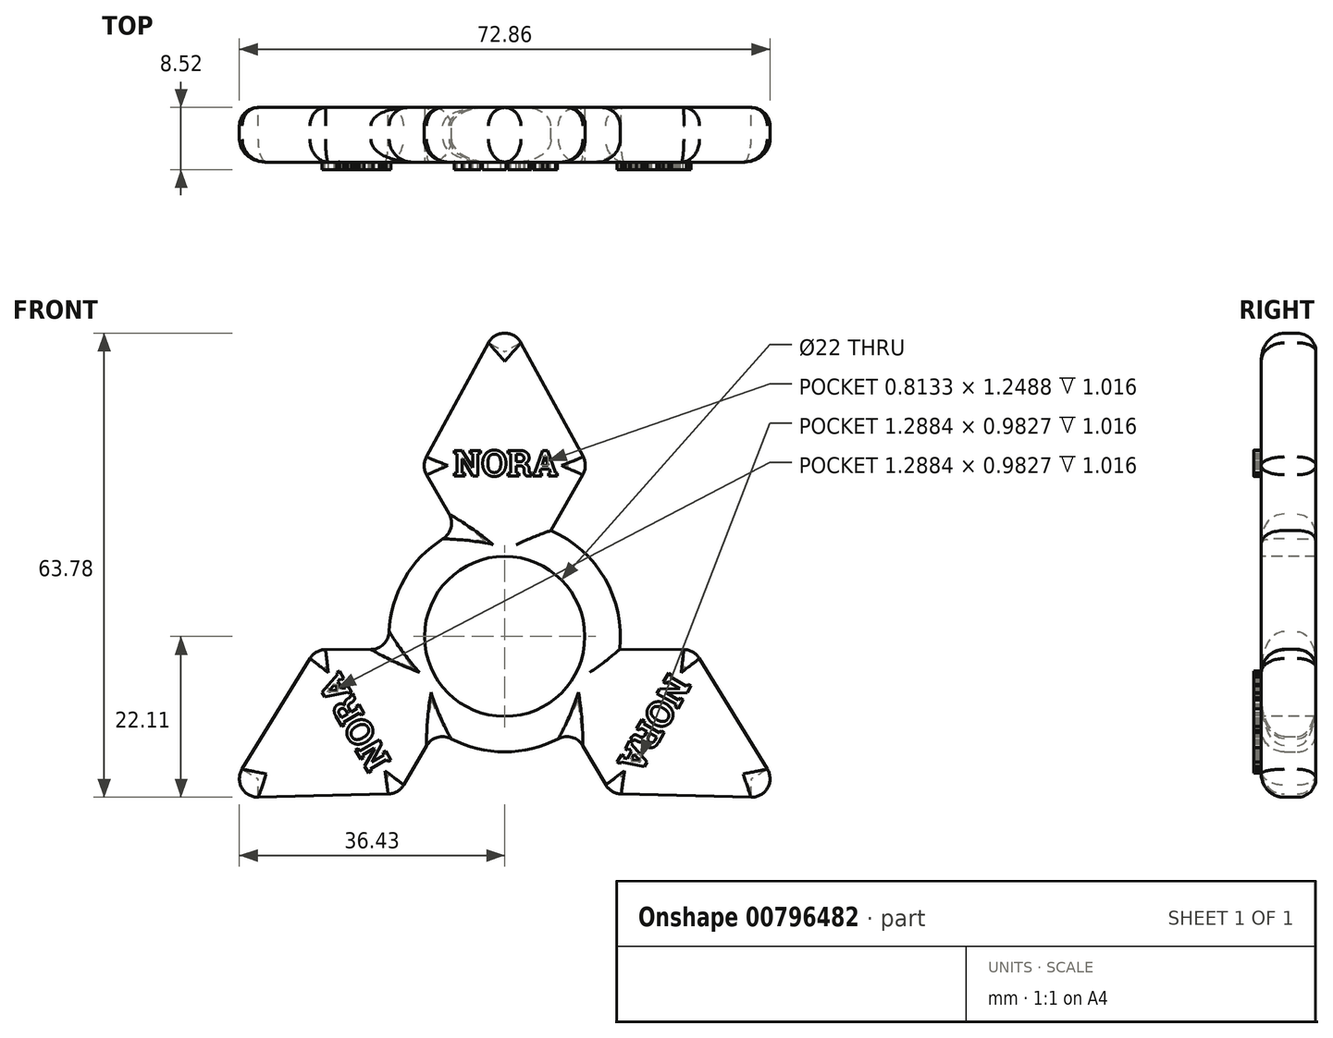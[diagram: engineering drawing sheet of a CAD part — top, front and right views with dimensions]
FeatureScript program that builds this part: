
annotation { "Feature Type Name" : "Feature", "Feature Type Description" : "" }
export const myFeature = defineFeature(function(context is Context, id is Id, definition is map)
    precondition{}
    {
        {
            var Q0;
            Q0=qCreatedBy(makeId("Front.planeOp"),FACE);
            var sketch = newSketch(context, id + "F0", { "sketchPlane" : qUnion([Q0])});
            skCircle(sketch, "E0", {"center": v(0, 0) * mm, "radius": 15.88 * mm});
            skSolve(sketch);
        }
        {
            var Q0;
            Q0 = qSketchRegion(id + "F0", true);
            extrude(context, id + "F1", {"entities" : qUnion([Q0]), "endBound" : BoundingType.SYMMETRIC, "depth" : 7.5 * mm, "offsetDistance" : 25.4 * mm});
        }
        {
            var Q0;
            Q0=qCreatedBy(makeId("Front.planeOp"),FACE);
            var sketch = newSketch(context, id + "F2", { "sketchPlane" : qUnion([Q0])});
            skLineSegment(sketch, "E1", {"start": v(-6.35, 14.55) * mm, "end": v(-11.43, 23.44) * mm});
            skLineSegment(sketch, "E2", {"start": v(-11.43, 23.44) * mm, "end": v(0, 44.45) * mm});
            skLineSegment(sketch, "E3", {"start": v(-17.44, 23.44) * mm, "end": v(16.7, 23.44) * mm, "construction": true});
            skLineSegment(sketch, "E4", {"start": v(0, 44.45) * mm, "end": v(11.43, 23.44) * mm});
            skLineSegment(sketch, "E5", {"start": v(11.43, 23.44) * mm, "end": v(6.35, 14.55) * mm});
            skLineSegment(sketch, "E6", {"start": v(0, 66.12) * mm, "end": v(0, -6.92) * mm, "construction": true});
            skLineSegment(sketch, "E7", {"start": v(-6.35, 14.55) * mm, "end": v(6.35, 14.55) * mm});
            skSolve(sketch);
        }
        {
            var Q0;
            Q0 = qSketchRegion(id + "F2", true);
            extrude(context, id + "F3", {"entities" : qUnion([Q0]), "endBound" : BoundingType.SYMMETRIC, "depth" : 7.5 * mm, "offsetDistance" : 25.4 * mm});
        }
        {
            var Q0;
            Q0=makeQuery(id+"F3.opExtrude","CAP_FACE",FACE,{"disambiguationData":[OSD([sQuery(id+"F2.wireOp",EDGE,"E1"),sQuery(id+"F2.wireOp",EDGE,"E2"),sQuery(id+"F2.wireOp",EDGE,"E4"),sQuery(id+"F2.wireOp",EDGE,"E5"),sQuery(id+"F2.wireOp",EDGE,"E7")])],"isStart":false});
            var sketch = newSketch(context, id + "F4", { "sketchPlane" : qUnion([Q0])});
            skText(sketch, "E8", { "text": "NORA", "fontName": "RobotoSlab-Bold.ttf"});
            const initialGuessF4  = {"E8": [-0.00705, 0.02202, 1, 0, 0.00359]};
            skSetInitialGuess(sketch, initialGuessF4);
            skSolve(sketch);
        }
        {
            var Q0;
            Q0 = qSketchRegion(id + "F4", true);
            extrude(context, id + "F5", {"entities" : qUnion([Q0]), "operationType" : NewBodyOperationType.ADD, "depth" : 1.02 * mm, "offsetDistance" : 25.4 * mm});
        }
        {
            var Q0;
            Q0=qCreatedBy(makeId("Top.planeOp"),FACE);
            var sketch = newSketch(context, id + "F6", { "sketchPlane" : qUnion([Q0])});
            skLineSegment(sketch, "E9", {"start": v(0, 50.9) * mm, "end": v(0, -46.74) * mm, "construction": true});
            skSolve(sketch);
        }
        {
            var Q0;
            Q0=makeQuery(id+"F3.opExtrude","SWEPT_BODY",BODY,{"disambiguationData":[OSD([sQuery(id+"F2.wireOp",EDGE,"E1"),sQuery(id+"F2.wireOp",EDGE,"E2"),sQuery(id+"F2.wireOp",EDGE,"E4"),sQuery(id+"F2.wireOp",EDGE,"E5"),sQuery(id+"F2.wireOp",EDGE,"E7")])]});
            var Q1;
            Q1=sQuery(id+"F6.wireOp",EDGE,"E9");
            circularPattern(context, id + "F7", {"entities" : qUnion([Q0]), "axis" : qUnion([Q1]), "angle" : 360 * degree, "instanceCount" : 3, "equalSpace" : true});
        }
        {
            var Q0;
            Q0=makeQuery(id+"F3.opExtrude","SWEPT_BODY",BODY,{"disambiguationData":[OSD([sQuery(id+"F2.wireOp",EDGE,"E1"),sQuery(id+"F2.wireOp",EDGE,"E2"),sQuery(id+"F2.wireOp",EDGE,"E4"),sQuery(id+"F2.wireOp",EDGE,"E5"),sQuery(id+"F2.wireOp",EDGE,"E7")])]});
            var Q1;
            Q1=makeQuery(id+"F1.opExtrude","SWEPT_BODY",BODY,{"disambiguationData":[OSD([sQuery(id+"F0.wireOp",EDGE,"E0")])]});
            var Q2;
            Q2=makeQuery(id+"F7.opPattern","COPY",BODY,{"derivedFrom":makeQuery(id+"F3.opExtrude","SWEPT_BODY",BODY,{"disambiguationData":[OSD([sQuery(id+"F2.wireOp",EDGE,"E1"),sQuery(id+"F2.wireOp",EDGE,"E2"),sQuery(id+"F2.wireOp",EDGE,"E4"),sQuery(id+"F2.wireOp",EDGE,"E5"),sQuery(id+"F2.wireOp",EDGE,"E7")])]}),"instanceName":"2"});
            var Q3;
            Q3=makeQuery(id+"F7.opPattern","COPY",BODY,{"derivedFrom":makeQuery(id+"F3.opExtrude","SWEPT_BODY",BODY,{"disambiguationData":[OSD([sQuery(id+"F2.wireOp",EDGE,"E1"),sQuery(id+"F2.wireOp",EDGE,"E2"),sQuery(id+"F2.wireOp",EDGE,"E4"),sQuery(id+"F2.wireOp",EDGE,"E5"),sQuery(id+"F2.wireOp",EDGE,"E7")])]}),"instanceName":"1"});
            booleanBodies(context, id + "F8", {"operationType" : BooleanOperationType.UNION, "tools" : qUnion([Q0, Q1, Q2, Q3])});
        }
        {
            var Q0;
            Q0=makeQuery(id+"F3.opExtrude","CAP_EDGE",EDGE,{"disambiguationData":[OSD([sQuery(id+"F2.wireOp",EDGE,"E4")])],"isStart":false});
            var Q1;
            Q1=makeQuery(id+"F3.opExtrude","CAP_EDGE",EDGE,{"disambiguationData":[OSD([sQuery(id+"F2.wireOp",EDGE,"E5")])],"isStart":false});
            var Q2;
            {var subQ0=sQuery(id+"F2.wireOp",EDGE,"E5");var subQ1=sQuery(id+"F0.wireOp",EDGE,"E0");Q2=makeQuery(id+"F8.opBoolean","SPLIT",EDGE,{"disambiguationData":[TD([makeQuery(id+"F3.opExtrude","SWEPT_FACE",FACE,{"disambiguationData":[OSD([subQ0])]})])],"derivedFrom":makeQuery(id+"F1.opExtrude","CAP_EDGE",EDGE,{"disambiguationData":[OSD([subQ1])],"isStart":false})});}
            var Q3;
            Q3=makeQuery(id+"F7.opPattern","COPY",EDGE,{"derivedFrom":makeQuery(id+"F3.opExtrude","CAP_EDGE",EDGE,{"disambiguationData":[OSD([sQuery(id+"F2.wireOp",EDGE,"E1")])],"isStart":false}),"instanceName":"2"});
            var Q4;
            Q4=makeQuery(id+"F7.opPattern","COPY",EDGE,{"derivedFrom":makeQuery(id+"F3.opExtrude","CAP_EDGE",EDGE,{"disambiguationData":[OSD([sQuery(id+"F2.wireOp",EDGE,"E2")])],"isStart":false}),"instanceName":"2"});
            var Q5;
            Q5=makeQuery(id+"F7.opPattern","COPY",EDGE,{"derivedFrom":makeQuery(id+"F3.opExtrude","CAP_EDGE",EDGE,{"disambiguationData":[OSD([sQuery(id+"F2.wireOp",EDGE,"E4")])],"isStart":false}),"instanceName":"2"});
            var Q6;
            Q6=makeQuery(id+"F7.opPattern","COPY",EDGE,{"derivedFrom":makeQuery(id+"F3.opExtrude","CAP_EDGE",EDGE,{"disambiguationData":[OSD([sQuery(id+"F2.wireOp",EDGE,"E5")])],"isStart":false}),"instanceName":"2"});
            var Q7;
            {var subQ0=sQuery(id+"F0.wireOp",EDGE,"E0");var subQ1=sQuery(id+"F2.wireOp",EDGE,"E1");Q7=makeQuery(id+"F8.opBoolean","SPLIT",EDGE,{"disambiguationData":[TD([makeQuery(id+"F7.opPattern","COPY",FACE,{"derivedFrom":makeQuery(id+"F3.opExtrude","SWEPT_FACE",FACE,{"disambiguationData":[OSD([subQ1])]}),"instanceName":"1"})])],"derivedFrom":makeQuery(id+"F1.opExtrude","CAP_EDGE",EDGE,{"disambiguationData":[OSD([subQ0])],"isStart":false})});}
            var Q8;
            Q8=makeQuery(id+"F7.opPattern","COPY",EDGE,{"derivedFrom":makeQuery(id+"F3.opExtrude","CAP_EDGE",EDGE,{"disambiguationData":[OSD([sQuery(id+"F2.wireOp",EDGE,"E1")])],"isStart":false}),"instanceName":"1"});
            var Q9;
            Q9=makeQuery(id+"F7.opPattern","COPY",EDGE,{"derivedFrom":makeQuery(id+"F3.opExtrude","CAP_EDGE",EDGE,{"disambiguationData":[OSD([sQuery(id+"F2.wireOp",EDGE,"E2")])],"isStart":false}),"instanceName":"1"});
            var Q10;
            Q10=makeQuery(id+"F7.opPattern","COPY",EDGE,{"derivedFrom":makeQuery(id+"F3.opExtrude","CAP_EDGE",EDGE,{"disambiguationData":[OSD([sQuery(id+"F2.wireOp",EDGE,"E4")])],"isStart":false}),"instanceName":"1"});
            var Q11;
            Q11=makeQuery(id+"F7.opPattern","COPY",EDGE,{"derivedFrom":makeQuery(id+"F3.opExtrude","CAP_EDGE",EDGE,{"disambiguationData":[OSD([sQuery(id+"F2.wireOp",EDGE,"E5")])],"isStart":false}),"instanceName":"1"});
            var Q12;
            {var subQ0=sQuery(id+"F2.wireOp",EDGE,"E1");var subQ1=sQuery(id+"F0.wireOp",EDGE,"E0");Q12=makeQuery(id+"F8.opBoolean","SPLIT",EDGE,{"disambiguationData":[TD([makeQuery(id+"F3.opExtrude","SWEPT_FACE",FACE,{"disambiguationData":[OSD([subQ0])]})])],"derivedFrom":makeQuery(id+"F1.opExtrude","CAP_EDGE",EDGE,{"disambiguationData":[OSD([subQ1])],"isStart":false})});}
            var Q13;
            Q13=makeQuery(id+"F3.opExtrude","CAP_EDGE",EDGE,{"disambiguationData":[OSD([sQuery(id+"F2.wireOp",EDGE,"E1")])],"isStart":false});
            var Q14;
            Q14=makeQuery(id+"F3.opExtrude","CAP_EDGE",EDGE,{"disambiguationData":[OSD([sQuery(id+"F2.wireOp",EDGE,"E2")])],"isStart":false});
            fillet(context, id + "F9", {"entities" : qUnion([Q0, Q1, Q2, Q3, Q4, Q5, Q6, Q7, Q8, Q9, Q10, Q11, Q12, Q13, Q14]), "radius" : 3.17 * mm, "tangentPropagation" : true, "allowEdgeOverflow" : false});
        }
        {
            var Q0;
            Q0=makeQuery(id+"F3.opExtrude","CAP_EDGE",EDGE,{"disambiguationData":[OSD([sQuery(id+"F2.wireOp",EDGE,"E2")])],"isStart":true});
            var Q1;
            Q1=makeQuery(id+"F3.opExtrude","CAP_EDGE",EDGE,{"disambiguationData":[OSD([sQuery(id+"F2.wireOp",EDGE,"E1")])],"isStart":true});
            var Q2;
            {var subQ1=sQuery(id+"F2.wireOp",EDGE,"E1");var subQ3=sQuery(id+"F0.wireOp",EDGE,"E0");Q2=makeQuery(id+"F8.opBoolean","SPLIT",EDGE,{"disambiguationData":[TD([makeQuery(id+"F3.opExtrude","SWEPT_FACE",FACE,{"disambiguationData":[OSD([subQ1])]})])],"derivedFrom":makeQuery(id+"F1.opExtrude","CAP_EDGE",EDGE,{"disambiguationData":[OSD([subQ3])],"isStart":true})});}
            var Q3;
            Q3=makeQuery(id+"F7.opPattern","COPY",EDGE,{"derivedFrom":makeQuery(id+"F3.opExtrude","CAP_EDGE",EDGE,{"disambiguationData":[OSD([sQuery(id+"F2.wireOp",EDGE,"E5")])],"isStart":true}),"instanceName":"1"});
            var Q4;
            Q4=makeQuery(id+"F7.opPattern","COPY",EDGE,{"derivedFrom":makeQuery(id+"F3.opExtrude","CAP_EDGE",EDGE,{"disambiguationData":[OSD([sQuery(id+"F2.wireOp",EDGE,"E4")])],"isStart":true}),"instanceName":"1"});
            var Q5;
            Q5=makeQuery(id+"F7.opPattern","COPY",EDGE,{"derivedFrom":makeQuery(id+"F3.opExtrude","CAP_EDGE",EDGE,{"disambiguationData":[OSD([sQuery(id+"F2.wireOp",EDGE,"E2")])],"isStart":true}),"instanceName":"1"});
            var Q6;
            Q6=makeQuery(id+"F7.opPattern","COPY",EDGE,{"derivedFrom":makeQuery(id+"F3.opExtrude","CAP_EDGE",EDGE,{"disambiguationData":[OSD([sQuery(id+"F2.wireOp",EDGE,"E1")])],"isStart":true}),"instanceName":"1"});
            var Q7;
            {var subQ0=sQuery(id+"F2.wireOp",EDGE,"E1");var subQ3=sQuery(id+"F0.wireOp",EDGE,"E0");Q7=makeQuery(id+"F8.opBoolean","SPLIT",EDGE,{"disambiguationData":[TD([makeQuery(id+"F7.opPattern","COPY",FACE,{"derivedFrom":makeQuery(id+"F3.opExtrude","SWEPT_FACE",FACE,{"disambiguationData":[OSD([subQ0])]}),"instanceName":"1"})])],"derivedFrom":makeQuery(id+"F1.opExtrude","CAP_EDGE",EDGE,{"disambiguationData":[OSD([subQ3])],"isStart":true})});}
            var Q8;
            Q8=makeQuery(id+"F7.opPattern","COPY",EDGE,{"derivedFrom":makeQuery(id+"F3.opExtrude","CAP_EDGE",EDGE,{"disambiguationData":[OSD([sQuery(id+"F2.wireOp",EDGE,"E5")])],"isStart":true}),"instanceName":"2"});
            var Q9;
            Q9=makeQuery(id+"F7.opPattern","COPY",EDGE,{"derivedFrom":makeQuery(id+"F3.opExtrude","CAP_EDGE",EDGE,{"disambiguationData":[OSD([sQuery(id+"F2.wireOp",EDGE,"E4")])],"isStart":true}),"instanceName":"2"});
            var Q10;
            Q10=makeQuery(id+"F7.opPattern","COPY",EDGE,{"derivedFrom":makeQuery(id+"F3.opExtrude","CAP_EDGE",EDGE,{"disambiguationData":[OSD([sQuery(id+"F2.wireOp",EDGE,"E2")])],"isStart":true}),"instanceName":"2"});
            var Q11;
            Q11=makeQuery(id+"F7.opPattern","COPY",EDGE,{"derivedFrom":makeQuery(id+"F3.opExtrude","CAP_EDGE",EDGE,{"disambiguationData":[OSD([sQuery(id+"F2.wireOp",EDGE,"E1")])],"isStart":true}),"instanceName":"2"});
            var Q12;
            {var subQ0=sQuery(id+"F2.wireOp",EDGE,"E5");var subQ3=sQuery(id+"F0.wireOp",EDGE,"E0");Q12=makeQuery(id+"F8.opBoolean","SPLIT",EDGE,{"disambiguationData":[TD([makeQuery(id+"F3.opExtrude","SWEPT_FACE",FACE,{"disambiguationData":[OSD([subQ0])]})])],"derivedFrom":makeQuery(id+"F1.opExtrude","CAP_EDGE",EDGE,{"disambiguationData":[OSD([subQ3])],"isStart":true})});}
            var Q13;
            Q13=makeQuery(id+"F3.opExtrude","CAP_EDGE",EDGE,{"disambiguationData":[OSD([sQuery(id+"F2.wireOp",EDGE,"E5")])],"isStart":true});
            var Q14;
            Q14=makeQuery(id+"F3.opExtrude","CAP_EDGE",EDGE,{"disambiguationData":[OSD([sQuery(id+"F2.wireOp",EDGE,"E4")])],"isStart":true});
            fillet(context, id + "F10", {"entities" : qUnion([Q0, Q1, Q2, Q3, Q4, Q5, Q6, Q7, Q8, Q9, Q10, Q11, Q12, Q13, Q14]), "radius" : 2.54 * mm, "tangentPropagation" : true, "allowEdgeOverflow" : false});
        }
        {
            var Q0;
            {var subQ0=sQuery(id+"F2.wireOp",EDGE,"E4");var subQ1=sQuery(id+"F2.wireOp",EDGE,"E7");var subQ2=sQuery(id+"F2.wireOp",EDGE,"E1");var subQ3=sQuery(id+"F2.wireOp",EDGE,"E5");var subQ4=sQuery(id+"F2.wireOp",EDGE,"E2");var subQ5=makeQuery(id+"F5.boolean.opBoolean","SPLIT",FACE,{"disambiguationData":[TD([makeQuery(id+"F3.opExtrude","SWEPT_FACE",FACE,{"disambiguationData":[OSD([subQ2])]})])],"derivedFrom":makeQuery(id+"F3.opExtrude","CAP_FACE",FACE,{"disambiguationData":[OSD([subQ2,subQ4,subQ0,subQ3,subQ1])],"isStart":false})});Q0=makeQuery(id+"F8.opBoolean","MERGE",FACE,{"derivedFrom":[makeQuery(id+"F1.opExtrude","CAP_FACE",FACE,{"disambiguationData":[OSD([sQuery(id+"F0.wireOp",EDGE,"E0")])],"isStart":false}),subQ5,makeQuery(id+"F7.opPattern","COPY",FACE,{"derivedFrom":subQ5,"instanceName":"1"}),makeQuery(id+"F7.opPattern","COPY",FACE,{"derivedFrom":subQ5,"instanceName":"2"})]});}
            var sketch = newSketch(context, id + "F11", { "sketchPlane" : qUnion([Q0])});
            skPoint(sketch, "E10", {"position": v(0, 0) * mm});
            skSolve(sketch);
        }
        {
            var Q0;
            Q0=sQuery(id+"F11.wireOp",VERTEX,"E10");
            var Q1;
            Q1=makeQuery(id+"F3.opExtrude","SWEPT_BODY",BODY,{"disambiguationData":[OSD([sQuery(id+"F2.wireOp",EDGE,"E1"),sQuery(id+"F2.wireOp",EDGE,"E2"),sQuery(id+"F2.wireOp",EDGE,"E4"),sQuery(id+"F2.wireOp",EDGE,"E5"),sQuery(id+"F2.wireOp",EDGE,"E7")])]});
            hole(context, id + "F12", {"style" : HoleStyle.SIMPLE, "endStyle" : HoleEndStyle.THROUGH, "holeDiameter" : 22 * mm, "majorDiameter" : 6.35 * mm, "isTappedThrough" : true, "tappedDepth" : 12.7 * mm, "tapClearance" : 3, "locations" : qUnion([Q0]), "scope" : qUnion([Q1])});
        }
        {
            var Q0;
            Q0=makeQuery(id+"F9.opFillet","BLEND_EDGE",EDGE,{"blendedFrom":[makeQuery(id+"F3.opExtrude","CAP_EDGE",EDGE,{"disambiguationData":[OSD([sQuery(id+"F2.wireOp",EDGE,"E2")])],"isStart":false}),makeQuery(id+"F3.opExtrude","CAP_EDGE",EDGE,{"disambiguationData":[OSD([sQuery(id+"F2.wireOp",EDGE,"E4")])],"isStart":false})],"blendedInto":[]});
            var Q1;
            Q1=makeQuery(id+"F7.opPattern","COPY",EDGE,{"derivedFrom":makeQuery(id+"F3.opExtrude","SWEPT_EDGE",EDGE,{"disambiguationData":[OSD([sQuery(id+"F2.wireOp",EDGE,"E2"),sQuery(id+"F2.wireOp",EDGE,"E4")])]}),"instanceName":"2"});
            var Q2;
            Q2=makeQuery(id+"F7.opPattern","COPY",EDGE,{"derivedFrom":makeQuery(id+"F3.opExtrude","SWEPT_EDGE",EDGE,{"disambiguationData":[OSD([sQuery(id+"F2.wireOp",EDGE,"E2"),sQuery(id+"F2.wireOp",EDGE,"E4")])]}),"instanceName":"1"});
            var Q3;
            Q3=makeQuery(id+"F3.opExtrude","SWEPT_EDGE",EDGE,{"disambiguationData":[OSD([sQuery(id+"F2.wireOp",EDGE,"E4"),sQuery(id+"F2.wireOp",EDGE,"E5")])]});
            var Q4;
            Q4=makeQuery(id+"F7.opPattern","COPY",EDGE,{"derivedFrom":makeQuery(id+"F3.opExtrude","SWEPT_EDGE",EDGE,{"disambiguationData":[OSD([sQuery(id+"F2.wireOp",EDGE,"E1"),sQuery(id+"F2.wireOp",EDGE,"E2")])]}),"instanceName":"2"});
            var Q5;
            Q5=makeQuery(id+"F3.opExtrude","SWEPT_EDGE",EDGE,{"disambiguationData":[OSD([sQuery(id+"F2.wireOp",EDGE,"E1"),sQuery(id+"F2.wireOp",EDGE,"E2")])]});
            var Q6;
            Q6=makeQuery(id+"F7.opPattern","COPY",EDGE,{"derivedFrom":makeQuery(id+"F3.opExtrude","SWEPT_EDGE",EDGE,{"disambiguationData":[OSD([sQuery(id+"F2.wireOp",EDGE,"E4"),sQuery(id+"F2.wireOp",EDGE,"E5")])]}),"instanceName":"1"});
            var Q7;
            Q7=makeQuery(id+"F7.opPattern","COPY",EDGE,{"derivedFrom":makeQuery(id+"F3.opExtrude","SWEPT_EDGE",EDGE,{"disambiguationData":[OSD([sQuery(id+"F2.wireOp",EDGE,"E1"),sQuery(id+"F2.wireOp",EDGE,"E2")])]}),"instanceName":"1"});
            var Q8;
            Q8=makeQuery(id+"F7.opPattern","COPY",EDGE,{"derivedFrom":makeQuery(id+"F3.opExtrude","SWEPT_EDGE",EDGE,{"disambiguationData":[OSD([sQuery(id+"F2.wireOp",EDGE,"E4"),sQuery(id+"F2.wireOp",EDGE,"E5")])]}),"instanceName":"2"});
            var Q9;
            Q9=makeQuery(id+"F3.opExtrude","SWEPT_EDGE",EDGE,{"disambiguationData":[OSD([sQuery(id+"F2.wireOp",EDGE,"E5"),sQuery(id+"F2.wireOp",EDGE,"E7")])]});
            var Q10;
            Q10=makeQuery(id+"F7.opPattern","COPY",EDGE,{"derivedFrom":makeQuery(id+"F3.opExtrude","SWEPT_EDGE",EDGE,{"disambiguationData":[OSD([sQuery(id+"F2.wireOp",EDGE,"E1"),sQuery(id+"F2.wireOp",EDGE,"E7")])]}),"instanceName":"2"});
            var Q11;
            Q11=makeQuery(id+"F7.opPattern","COPY",EDGE,{"derivedFrom":makeQuery(id+"F3.opExtrude","SWEPT_EDGE",EDGE,{"disambiguationData":[OSD([sQuery(id+"F2.wireOp",EDGE,"E1"),sQuery(id+"F2.wireOp",EDGE,"E7")])]}),"instanceName":"1"});
            var Q12;
            Q12=makeQuery(id+"F7.opPattern","COPY",EDGE,{"derivedFrom":makeQuery(id+"F3.opExtrude","SWEPT_EDGE",EDGE,{"disambiguationData":[OSD([sQuery(id+"F2.wireOp",EDGE,"E5"),sQuery(id+"F2.wireOp",EDGE,"E7")])]}),"instanceName":"2"});
            var Q13;
            Q13=makeQuery(id+"F3.opExtrude","SWEPT_EDGE",EDGE,{"disambiguationData":[OSD([sQuery(id+"F2.wireOp",EDGE,"E1"),sQuery(id+"F2.wireOp",EDGE,"E7")])]});
            var Q14;
            Q14=makeQuery(id+"F7.opPattern","COPY",EDGE,{"derivedFrom":makeQuery(id+"F3.opExtrude","SWEPT_EDGE",EDGE,{"disambiguationData":[OSD([sQuery(id+"F2.wireOp",EDGE,"E5"),sQuery(id+"F2.wireOp",EDGE,"E7")])]}),"instanceName":"1"});
            fillet(context, id + "F13", {"entities" : qUnion([Q0, Q1, Q2, Q3, Q4, Q5, Q6, Q7, Q8, Q9, Q10, Q11, Q12, Q13, Q14]), "radius" : 2.54 * mm, "tangentPropagation" : true, "allowEdgeOverflow" : false});
        }
    });
